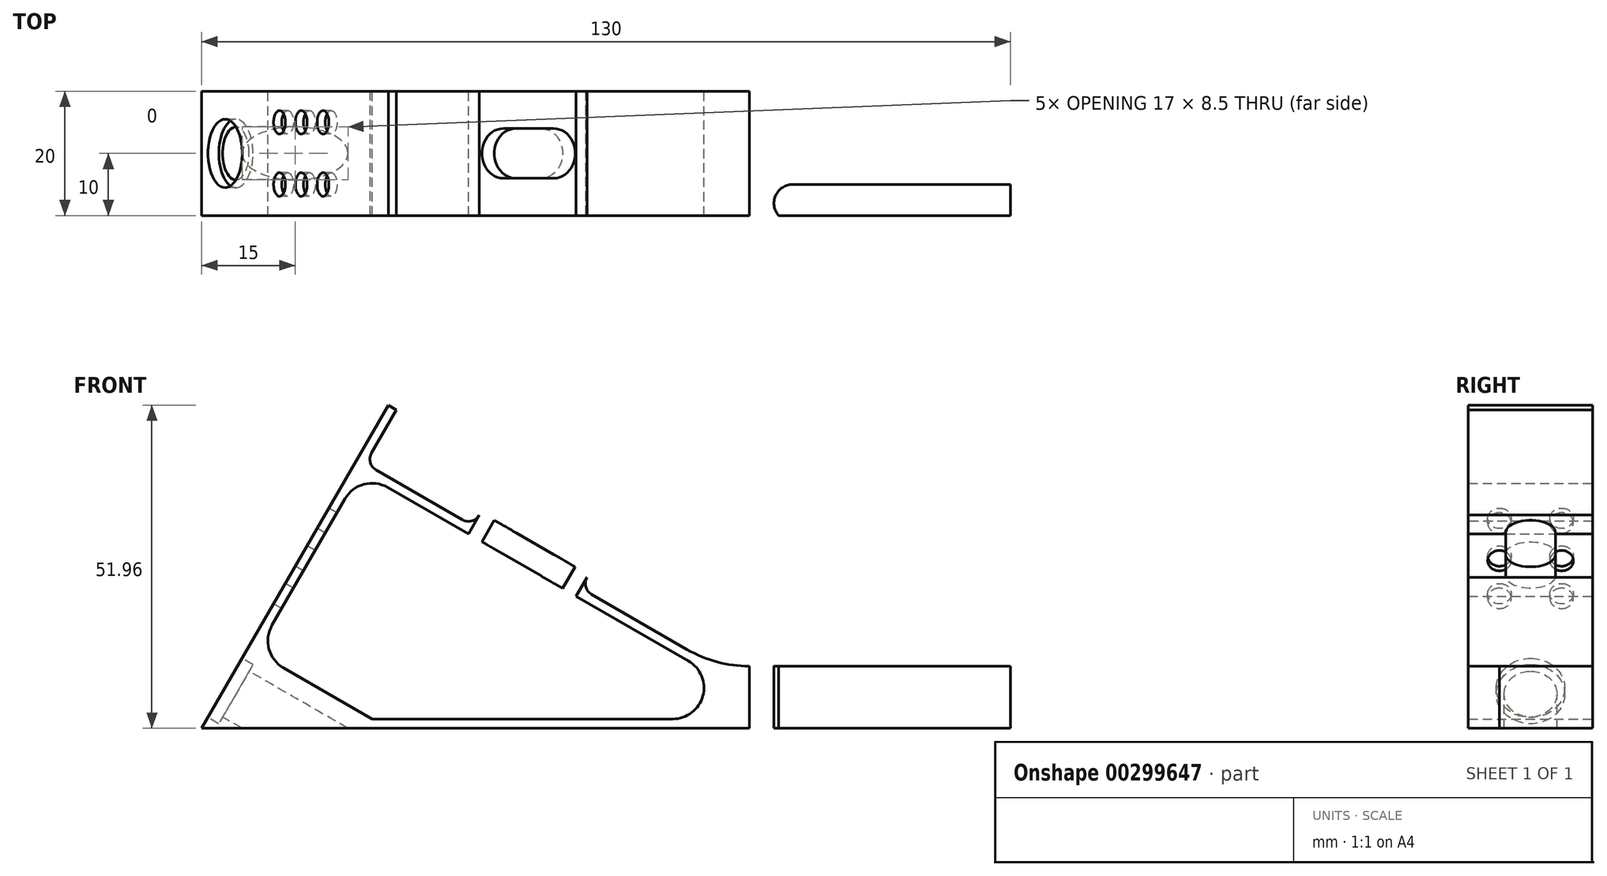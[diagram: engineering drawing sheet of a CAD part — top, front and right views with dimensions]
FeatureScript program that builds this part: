
annotation { "Feature Type Name" : "Feature", "Feature Type Description" : "" }
export const myFeature = defineFeature(function(context is Context, id is Id, definition is map)
    precondition{}
    {
        {
            var Q0;
            Q0=qCreatedBy(makeId("Front.planeOp"),FACE);
            var sketch = newSketch(context, id + "F0", { "sketchPlane" : qUnion([Q0])});
            skLineSegment(sketch, "E0", {"start": v(0, 0) * mm, "end": v(30, 51.96) * mm});
            skLineSegment(sketch, "E1", {"start": v(30, 51.96) * mm, "end": v(31.3, 51.21) * mm});
            skLineSegment(sketch, "E2", {"start": v(31.3, 51.21) * mm, "end": v(26.3, 42.55) * mm});
            skLineSegment(sketch, "E3", {"start": v(26.3, 42.55) * mm, "end": v(43.62, 32.55) * mm});
            skArc(sketch, "E4", {"start": v(75.73, 1.5) * mm, "mid": v(80.56, 5.2) * mm, "end": v(78.23, 10.83) * mm});
            skLineSegment(sketch, "E5", {"start": v(78.23, 10.83) * mm, "end": v(29.88, 38.75) * mm});
            skArc(sketch, "E6", {"start": v(29.88, 38.75) * mm, "mid": v(26.08, 39.25) * mm, "end": v(23.05, 36.92) * mm});
            skLineSegment(sketch, "E7", {"start": v(23.05, 36.92) * mm, "end": v(11.3, 16.57) * mm});
            skArc(sketch, "E8", {"start": v(11.3, 16.57) * mm, "mid": v(10.8, 12.77) * mm, "end": v(13.13, 9.74) * mm});
            skLineSegment(sketch, "E9", {"start": v(88.03, 10) * mm, "end": v(130, 10) * mm});
            skLineSegment(sketch, "E10", {"start": v(130, 10) * mm, "end": v(130, 0) * mm});
            skLineSegment(sketch, "E11", {"start": v(13.13, 9.74) * mm, "end": v(27.38, 1.5) * mm});
            skLineSegment(sketch, "E12", {"start": v(0, 0) * mm, "end": v(130, 0) * mm});
            skLineSegment(sketch, "E13", {"start": v(27.38, 1.5) * mm, "end": v(75.73, 1.5) * mm});
            skLineSegment(sketch, "E14", {"start": v(43.62, 32.55) * mm, "end": v(44.87, 34.71) * mm});
            skLineSegment(sketch, "E15", {"start": v(44.87, 34.71) * mm, "end": v(62.19, 24.71) * mm});
            skLineSegment(sketch, "E16", {"start": v(62.19, 24.71) * mm, "end": v(60.94, 22.55) * mm});
            skLineSegment(sketch, "E17", {"start": v(60.94, 22.55) * mm, "end": v(78.03, 12.68) * mm});
            skArc(sketch, "E18", {"start": v(78.03, 12.68) * mm, "mid": v(82.86, 10.68) * mm, "end": v(88.03, 10) * mm});
            skSolve(sketch);
        }
        {
            var Q0;
            Q0=makeQuery(id+"F0.imprint","IMPRINT",FACE,{"disambiguationData":[TD([[makeQuery(id+"F0.imprint","IMPRINT",EDGE,{"derivedFrom":sQuery(id+"F0.wireOp",EDGE,"E0")}),-1.0]])]});
            extrude(context, id + "F1", {"entities" : qUnion([Q0]), "endBound" : BoundingType.SYMMETRIC, "depth" : 20 * mm});
        }
        {
            var Q0;
            Q0=makeQuery(id+"F1.opExtrude","SWEPT_FACE",FACE,{"disambiguationData":[OSD([sQuery(id+"F0.wireOp",EDGE,"E9")])]});
            var sketch = newSketch(context, id + "F2", { "sketchPlane" : qUnion([Q0])});
            skLineSegment(sketch, "E19", {"start": v(130, 0) * mm, "end": v(88.03, 0) * mm, "construction": true});
            skLineSegment(sketch, "E20", {"start": v(95, 5) * mm, "end": v(130, 5) * mm});
            skArc(sketch, "E21", {"start": v(92.76, 10) * mm, "mid": v(92.26, 6.78) * mm, "end": v(95, 5) * mm});
            skLineSegment(sketch, "E22", {"start": v(92.76, 10) * mm, "end": v(130, 10) * mm});
            skLineSegment(sketch, "E23", {"start": v(130, 10) * mm, "end": v(130, 5) * mm});
            skArc(sketch, "E24.MirrorCS", {"start": v(92.76, -10) * mm, "mid": v(92.26, -6.78) * mm, "end": v(95, -5) * mm});
            skLineSegment(sketch, "E25.MirrorCS", {"start": v(95, -5) * mm, "end": v(130, -5) * mm});
            skLineSegment(sketch, "E26.MirrorCS", {"start": v(92.76, -10) * mm, "end": v(130, -10) * mm});
            skLineSegment(sketch, "E27.MirrorCS", {"start": v(130, -10) * mm, "end": v(130, -5) * mm});
            skLineSegment(sketch, "E28", {"start": v(130, -3) * mm, "end": v(113, -3) * mm});
            skLineSegment(sketch, "E29", {"start": v(130, 3) * mm, "end": v(113, 3) * mm});
            skArc(sketch, "E30", {"start": v(113, 3) * mm, "mid": v(110, 0) * mm, "end": v(113, -3) * mm});
            skSolve(sketch);
        }
        {
            var Q0;
            Q0=makeQuery(id+"F2.imprint","IMPRINT",FACE,{"disambiguationData":[TD([[makeQuery(id+"F2.imprint","IMPRINT",EDGE,{"derivedFrom":sQuery(id+"F2.wireOp",EDGE,"E24.MirrorCS")}),-1.0]])]});
            var Q1;
            Q1=makeQuery(id+"F2.imprint","IMPRINT",FACE,{"disambiguationData":[TD([[makeQuery(id+"F2.imprint","IMPRINT",EDGE,{"derivedFrom":sQuery(id+"F2.wireOp",EDGE,"E20")}),1.0]])]});
            var Q2;
            {var subQ0=sQuery(id+"F2.wireOp",EDGE,"E28");Q2=makeQuery(id+"F2.imprint","IMPRINT",FACE,{"disambiguationData":[TD([[makeQuery(id+"F2.imprint","IMPRINT",EDGE,{"derivedFrom":subQ0}),-1.0]])]});}
            extrude(context, id + "F3", {"entities" : qUnion([Q0, Q1, Q2]), "operationType" : NewBodyOperationType.REMOVE, "endBound" : BoundingType.THROUGH_ALL, "oppositeDirection" : true, "depth" : 25 * mm});
        }
        {
            var Q0;
            Q0=makeQuery(id+"F1.opExtrude","SWEPT_FACE",FACE,{"disambiguationData":[OSD([sQuery(id+"F0.wireOp",EDGE,"E0")])]});
            var sketch = newSketch(context, id + "F4", { "sketchPlane" : qUnion([Q0])});
            skCircle(sketch, "E31", {"center": v(0, 7.5) * mm, "radius": 5.5 * mm});
            skCircle(sketch, "E32", {"center": v(0, 7.5) * mm, "radius": 4.25 * mm});
            skCircle(sketch, "E33", {"center": v(-5, 39) * mm, "radius": 1.9 * mm});
            skLineSegment(sketch, "E34", {"start": v(0, 0) * mm, "end": v(0, 80.53) * mm, "construction": true});
            skPoint(sketch, "E34.endSnap0", {"position": v(0, 60) * mm});
            skCircle(sketch, "E35.0.1.0", {"center": v(-5, 32) * mm, "radius": 1.9 * mm});
            skCircle(sketch, "E35.0.2.0", {"center": v(-5, 25) * mm, "radius": 1.9 * mm});
            skCircle(sketch, "E35.1.0.0", {"center": v(5, 39) * mm, "radius": 1.9 * mm});
            skCircle(sketch, "E35.1.1.0", {"center": v(5, 32) * mm, "radius": 1.9 * mm});
            skCircle(sketch, "E35.1.2.0", {"center": v(5, 25) * mm, "radius": 1.9 * mm});
            skLineSegment(sketch, "E35.direction1", {"start": v(-5, 39) * mm, "end": v(5, 39) * mm, "construction": true});
            skLineSegment(sketch, "E35.direction2", {"start": v(-5, 39) * mm, "end": v(-5, 32) * mm, "construction": true});
            skSolve(sketch);
        }
        {
            var Q0;
            Q0=sQuery(id+"F4.wireOp",VERTEX,"E32.center");
            var Q1;
            Q1=makeQuery(id+"F1.opExtrude","SWEPT_BODY",BODY,{"disambiguationData":[OSD([sQuery(id+"F0.wireOp",EDGE,"E0"),sQuery(id+"F0.wireOp",EDGE,"E1"),sQuery(id+"F0.wireOp",EDGE,"E2"),sQuery(id+"F0.wireOp",EDGE,"E3"),sQuery(id+"F0.wireOp",EDGE,"E4"),sQuery(id+"F0.wireOp",EDGE,"E5"),sQuery(id+"F0.wireOp",EDGE,"E6"),sQuery(id+"F0.wireOp",EDGE,"E7"),sQuery(id+"F0.wireOp",EDGE,"E8"),sQuery(id+"F0.wireOp",EDGE,"E9"),sQuery(id+"F0.wireOp",EDGE,"E10"),sQuery(id+"F0.wireOp",EDGE,"E11"),sQuery(id+"F0.wireOp",EDGE,"E12"),sQuery(id+"F0.wireOp",EDGE,"E13"),sQuery(id+"F0.wireOp",EDGE,"E14"),sQuery(id+"F0.wireOp",EDGE,"E15"),sQuery(id+"F0.wireOp",EDGE,"E16"),sQuery(id+"F0.wireOp",EDGE,"E17"),sQuery(id+"F0.wireOp",EDGE,"E18")])]});
            hole(context, id + "F5", {"style" : HoleStyle.C_BORE, "endStyle" : HoleEndStyle.THROUGH, "holeDiameter" : 8.5 * mm, "cBoreDiameter" : 11 * mm, "cBoreDepth" : 2 * mm, "tappedDepth" : 12 * mm, "tapClearance" : 3, "locations" : qUnion([Q0]), "scope" : qUnion([Q1])});
        }
        {
            var Q0;
            Q0=makeQuery(id+"F4.imprint","IMPRINT",FACE,{"disambiguationData":[TD([[makeQuery(id+"F4.imprint","IMPRINT",EDGE,{"derivedFrom":sQuery(id+"F4.wireOp",EDGE,"E33")}),1.0]])]});
            var Q1;
            Q1=makeQuery(id+"F4.imprint","IMPRINT",FACE,{"disambiguationData":[TD([[makeQuery(id+"F4.imprint","IMPRINT",EDGE,{"derivedFrom":sQuery(id+"F4.wireOp",EDGE,"E35.1.0.0")}),1.0]])]});
            var Q2;
            Q2=makeQuery(id+"F4.imprint","IMPRINT",FACE,{"disambiguationData":[TD([[makeQuery(id+"F4.imprint","IMPRINT",EDGE,{"derivedFrom":sQuery(id+"F4.wireOp",EDGE,"E35.0.1.0")}),1.0]])]});
            var Q3;
            Q3=makeQuery(id+"F4.imprint","IMPRINT",FACE,{"disambiguationData":[TD([[makeQuery(id+"F4.imprint","IMPRINT",EDGE,{"derivedFrom":sQuery(id+"F4.wireOp",EDGE,"E35.1.1.0")}),1.0]])]});
            var Q4;
            Q4=makeQuery(id+"F4.imprint","IMPRINT",FACE,{"disambiguationData":[TD([[makeQuery(id+"F4.imprint","IMPRINT",EDGE,{"derivedFrom":sQuery(id+"F4.wireOp",EDGE,"E35.0.2.0")}),1.0]])]});
            var Q5;
            Q5=makeQuery(id+"F4.imprint","IMPRINT",FACE,{"disambiguationData":[TD([[makeQuery(id+"F4.imprint","IMPRINT",EDGE,{"derivedFrom":sQuery(id+"F4.wireOp",EDGE,"E35.1.2.0")}),1.0]])]});
            extrude(context, id + "F6", {"entities" : qUnion([Q0, Q1, Q2, Q3, Q4, Q5]), "operationType" : NewBodyOperationType.REMOVE, "endBound" : BoundingType.UP_TO_NEXT, "oppositeDirection" : true, "depth" : 25 * mm});
        }
        {
            var Q0;
            Q0=makeQuery(id+"F1.opExtrude","SWEPT_EDGE",EDGE,{"disambiguationData":[OSD([sQuery(id+"F0.wireOp",EDGE,"E3"),sQuery(id+"F0.wireOp",EDGE,"E14")])]});
            var Q1;
            Q1=makeQuery(id+"F1.opExtrude","SWEPT_EDGE",EDGE,{"disambiguationData":[OSD([sQuery(id+"F0.wireOp",EDGE,"E16"),sQuery(id+"F0.wireOp",EDGE,"E17")])]});
            var Q2;
            Q2=makeQuery(id+"F1.opExtrude","SWEPT_EDGE",EDGE,{"disambiguationData":[OSD([sQuery(id+"F0.wireOp",EDGE,"E2"),sQuery(id+"F0.wireOp",EDGE,"E3")])]});
            fillet(context, id + "F7", {"entities" : qUnion([Q0, Q1, Q2]), "radius" : 2 * mm, "tangentPropagation" : true, "allowEdgeOverflow" : false});
        }
        {
            var Q0;
            Q0=makeQuery(id+"F1.opExtrude","SWEPT_FACE",FACE,{"disambiguationData":[OSD([sQuery(id+"F0.wireOp",EDGE,"E15")])]});
            var sketch = newSketch(context, id + "F8", { "sketchPlane" : qUnion([Q0])});
            skLineSegment(sketch, "E36", {"start": v(28, 0) * mm, "end": v(35, 0) * mm, "construction": true});
            skArc(sketch, "E37.0.startCap", {"start": v(28, -4) * mm, "mid": v(24, 0) * mm, "end": v(28, 4) * mm});
            skArc(sketch, "E37.0.endCap", {"start": v(35, 4) * mm, "mid": v(39, 0) * mm, "end": v(35, -4) * mm});
            skLineSegment(sketch, "E37.0.left", {"start": v(28, 4) * mm, "end": v(35, 4) * mm});
            skLineSegment(sketch, "E37.0.right", {"start": v(28, -4) * mm, "end": v(35, -4) * mm});
            skPoint(sketch, "E38", {"position": v(21.5, 0) * mm});
            skSolve(sketch);
        }
        {
            var Q0;
            Q0=makeQuery(id+"F8.imprint","IMPRINT",FACE,{"disambiguationData":[TD([[makeQuery(id+"F8.imprint","IMPRINT",EDGE,{"derivedFrom":sQuery(id+"F8.wireOp",EDGE,"E37.0.startCap")}),-1.0]])]});
            extrude(context, id + "F9", {"entities" : qUnion([Q0]), "operationType" : NewBodyOperationType.REMOVE, "endBound" : BoundingType.UP_TO_NEXT, "oppositeDirection" : true, "depth" : 25 * mm});
        }
    });
